# Revit family: DEVIreg Room_RFA_1
name_source: partatom
category: Data Devices
units: mm (PartAtom-declared; Revit-internal decimal feet)

## family parameters
Cut with Voids When Loaded = No
Host = Face
Maintain Annotation Orientation = No
OmniClass Number = 23.85.50.17
OmniClass Title = Communication and Data Processing Equipment
Part Type = Normal
Room Calculation Point = No
Round Connector Dimension = Use Diameter
Shared = No

## types (1)
- DEVIreg™ Room_140F1161
    Ambient Temperature Range = 0 °C to 30 °C
    Ball pressure test temperature = 75 °C
    Battery back-up time, min = 60
    Body Material = Danfoss Plastic White
    Cable specification for connector terminals, max. = 1 x 4 mm² or 2 x 2.5 mm²
    Controller type = 1 B
    D = 22 mm  [stored 0.0721785 ft]
    Default Elevation = 0 mm  [stored 0 ft]
    Description = Programmable timer thermostat
    Frost protection = 4 °C - 14 °C (default 5 °C)
    H = 85 mm  [stored 0.278871 ft]
    IP Rating = 21
    IfcExportAs = IfcElectricApplianceType
    IfcExportType = DEVIreg Room
    Immunity against voltage surges = Over Voltage Category III
    In-wall depth = 22 mm  [stored 0.0721785 ft]
    Inductive load = Cos Φ = 0.3 max. 1A
    L = 22 mm  [stored 0.0721785 ft]
    LOD 200 = No
    LOD 350 = Yes
    Manufacturer = Danfoss
    Model = 140F1161
    Model Type = DEVIreg™ Room
    Mounting method = In-wall
    NominalHeight = 85 mm  [stored 0.278871 ft]
    NominalLength = 22 mm  [stored 0.0721785 ft]
    NominalWidth = 85 mm  [stored 0.278871 ft]
    OF1 = 15 mm
    OF2 = 20 mm  [stored 0.0656168 ft]
    Operating Temperature Range = 0 °C to 35 °C, 90% RH non-condensing
    Pollution degree = 2 (domestic use)
    Power = 0 W
    Protection class = Class II
    R = 20 mm  [stored 0.0656168 ft]
    Regulation = PWM - Pulse Width Modulation
    Resistive load = 16A / 3680W @ 230V
    Sensing unit = NTC 15 kΩ @ 25 °C, 3 m. (default),
NTC 2 kΩ @ 25 °C
NTC 6.8 kΩ @ 25 °C,
NTC 10 kΩ @ 25 °C,
NTC 12 kΩ @ 25 °C,
NTC 33 kΩ @ 25 °C,
NTC 47 kΩ @ 25 °C
    Software class = A
    Standby power consumption = 0.2 W
    Storage temperature = -25 °C to 60 °C, 90% RH non-condensing
    URL = https://store.danfoss.com
    Voltage = 230 V
    W = 85 mm  [stored 0.278871 ft]
    Weight = 0.20 kg
    r = 2 mm  [stored 0.00656168 ft]

note: [stored X ft] marks values corroborated as IEEE doubles in the binary element streams (Revit-internal decimal feet)

## geometry (parser evidence)
native form markers: Sweep x1
no freeform markers — native parametric forms only
